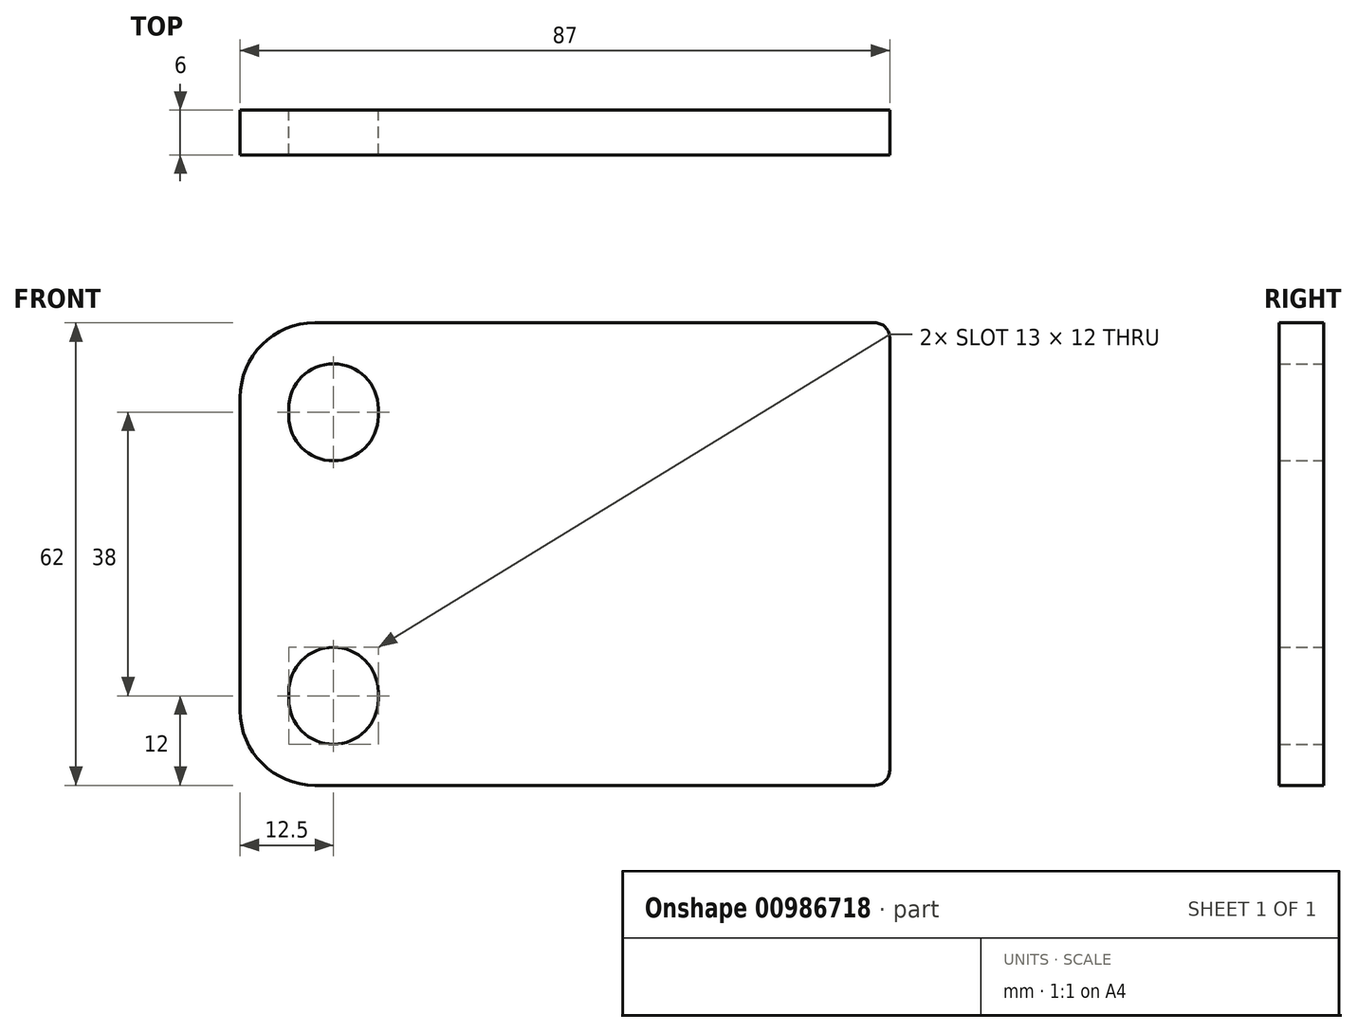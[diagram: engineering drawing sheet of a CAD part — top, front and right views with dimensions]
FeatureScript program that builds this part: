
annotation { "Feature Type Name" : "Feature", "Feature Type Description" : "" }
export const myFeature = defineFeature(function(context is Context, id is Id, definition is map)
    precondition{}
    {
        {
            var Q0;
            Q0=qCreatedBy(makeId("Front.planeOp"),FACE);
            var sketch = newSketch(context, id + "F0", { "sketchPlane" : qUnion([Q0])});
            skLineSegment(sketch, "E0.bottom", {"start": v(-33.5, -31) * mm, "end": v(41.5, -31) * mm});
            skLineSegment(sketch, "E0.top", {"start": v(-33.5, 31) * mm, "end": v(41.5, 31) * mm});
            skLineSegment(sketch, "E0.left", {"start": v(-43.5, -21) * mm, "end": v(-43.5, 21) * mm});
            skLineSegment(sketch, "E0.right", {"start": v(43.5, -29) * mm, "end": v(43.5, 29) * mm});
            skPoint(sketch, "E0.middle", {"position": v(0, 0) * mm});
            skLineSegment(sketch, "E1", {"start": v(-43.5, 31) * mm, "end": v(-43.5, 18.5) * mm, "construction": true});
            skLineSegment(sketch, "E2", {"start": v(-43.5, 18.5) * mm, "end": v(-31, 18.5) * mm, "construction": true});
            skLineSegment(sketch, "E3", {"start": v(-31, 18.5) * mm, "end": v(-31, -18.5) * mm, "construction": true});
            skPoint(sketch, "E4.visualSharp", {"position": v(-43.5, 31) * mm});
            skArc(sketch, "E4.filletArc", {"start": v(-33.5, 31) * mm, "mid": v(-40.57, 28.07) * mm, "end": v(-43.5, 21) * mm});
            skPoint(sketch, "E5.visualSharp", {"position": v(-43.5, -31) * mm});
            skArc(sketch, "E5.filletArc", {"start": v(-43.5, -21) * mm, "mid": v(-40.57, -28.07) * mm, "end": v(-33.5, -31) * mm});
            skPoint(sketch, "E6.visualSharp", {"position": v(43.5, 31) * mm});
            skArc(sketch, "E6.filletArc", {"start": v(43.5, 29) * mm, "mid": v(42.91, 30.41) * mm, "end": v(41.5, 31) * mm});
            skPoint(sketch, "E7.visualSharp", {"position": v(43.5, -31) * mm});
            skArc(sketch, "E7.filletArc", {"start": v(41.5, -31) * mm, "mid": v(42.91, -30.41) * mm, "end": v(43.5, -29) * mm});
            skArc(sketch, "E8", {"start": v(-25, -18.5) * mm, "mid": v(-31, -12.5) * mm, "end": v(-37, -18.5) * mm});
            skArc(sketch, "E9", {"start": v(-37, 18.5) * mm, "mid": v(-31, 12.5) * mm, "end": v(-25, 18.5) * mm});
            skLineSegment(sketch, "E10", {"start": v(-31, 18.5) * mm, "end": v(-31, 19.5) * mm, "construction": true});
            skArc(sketch, "E11", {"start": v(-25, 19.5) * mm, "mid": v(-31, 25.5) * mm, "end": v(-37, 19.5) * mm});
            skLineSegment(sketch, "E12", {"start": v(-37, 18.5) * mm, "end": v(-37, 19.5) * mm});
            skLineSegment(sketch, "E13", {"start": v(-25, 19.5) * mm, "end": v(-25, 18.5) * mm});
            skArc(sketch, "E14", {"start": v(-37, -19.5) * mm, "mid": v(-31, -25.5) * mm, "end": v(-25, -19.5) * mm});
            skLineSegment(sketch, "E15", {"start": v(-25, -19.5) * mm, "end": v(-25, -18.5) * mm});
            skLineSegment(sketch, "E16", {"start": v(-37, -19.5) * mm, "end": v(-37, -18.5) * mm});
            skLineSegment(sketch, "E17", {"start": v(-31, -18.5) * mm, "end": v(-31, -19.5) * mm});
            skSolve(sketch);
        }
        {
            var Q0;
            Q0=makeQuery(id+"F0.imprint","IMPRINT",FACE,{"disambiguationData":[TD([[makeQuery(id+"F0.imprint","IMPRINT",EDGE,{"derivedFrom":sQuery(id+"F0.wireOp",EDGE,"E0.bottom")}),1.0]])]});
            extrude(context, id + "F1", {"entities" : qUnion([Q0]), "depth" : 6 * mm, "offsetDistance" : 25 * mm});
        }
    });
